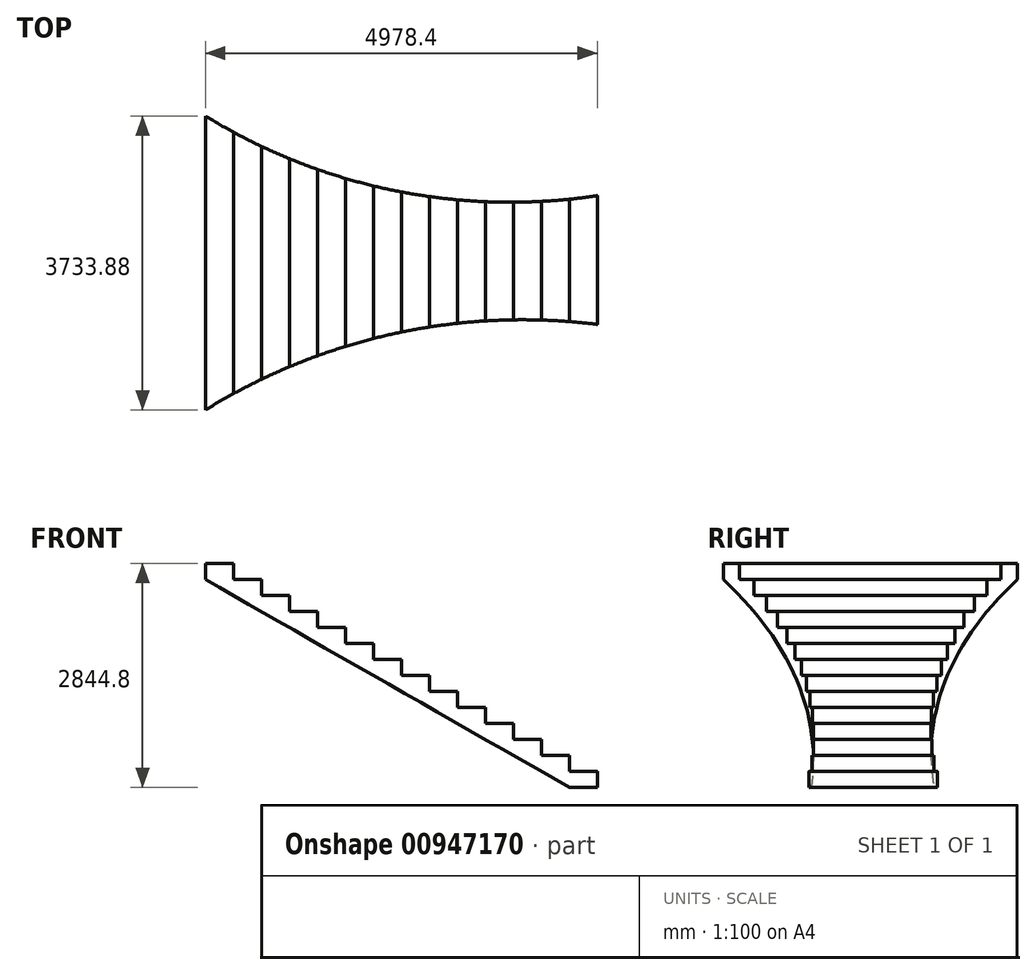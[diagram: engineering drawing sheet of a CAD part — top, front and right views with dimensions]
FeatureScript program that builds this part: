
annotation { "Feature Type Name" : "Feature", "Feature Type Description" : "" }
export const myFeature = defineFeature(function(context is Context, id is Id, definition is map)
    precondition{}
    {
        {
            var Q0;
            Q0=qCreatedBy(makeId("Front.planeOp"),FACE);
            var sketch = newSketch(context, id + "F0", { "sketchPlane" : qUnion([Q0])});
            skLineSegment(sketch, "E0", {"start": v(0, 0) * mm, "end": v(0, 203.2) * mm});
            skLineSegment(sketch, "E1", {"start": v(0, 203.2) * mm, "end": v(-355.6, 203.2) * mm});
            skLineSegment(sketch, "E2", {"start": v(-355.6, 203.2) * mm, "end": v(-355.6, 406.4) * mm});
            skLineSegment(sketch, "E3", {"start": v(-355.6, 406.4) * mm, "end": v(-711.2, 406.4) * mm});
            skLineSegment(sketch, "E4", {"start": v(-711.2, 406.4) * mm, "end": v(-711.2, 609.6) * mm});
            skLineSegment(sketch, "E5", {"start": v(-711.2, 609.6) * mm, "end": v(-1066.8, 609.6) * mm});
            skLineSegment(sketch, "E6", {"start": v(-1066.8, 609.6) * mm, "end": v(-1066.8, 812.8) * mm});
            skLineSegment(sketch, "E7", {"start": v(-1066.8, 812.8) * mm, "end": v(-1422.4, 812.8) * mm});
            skLineSegment(sketch, "E8", {"start": v(-1422.4, 812.8) * mm, "end": v(-1422.4, 1016) * mm});
            skLineSegment(sketch, "E9", {"start": v(-1422.4, 1016) * mm, "end": v(-1778, 1016) * mm});
            skLineSegment(sketch, "E10", {"start": v(-1778, 1016) * mm, "end": v(-1778, 1219.2) * mm});
            skLineSegment(sketch, "E11", {"start": v(-1778, 1219.2) * mm, "end": v(-2133.6, 1219.2) * mm});
            skLineSegment(sketch, "E12", {"start": v(-2133.6, 1219.2) * mm, "end": v(-2133.6, 1422.4) * mm});
            skLineSegment(sketch, "E13", {"start": v(-2133.6, 1422.4) * mm, "end": v(-2489.2, 1422.4) * mm});
            skLineSegment(sketch, "E14", {"start": v(-2489.2, 1422.4) * mm, "end": v(-2489.2, 1625.6) * mm});
            skLineSegment(sketch, "E15", {"start": v(-2489.2, 1625.6) * mm, "end": v(-2844.8, 1625.6) * mm});
            skLineSegment(sketch, "E16", {"start": v(-2844.8, 1625.6) * mm, "end": v(-2844.8, 1828.8) * mm});
            skLineSegment(sketch, "E17", {"start": v(-2844.8, 1828.8) * mm, "end": v(-3200.4, 1828.8) * mm});
            skLineSegment(sketch, "E18", {"start": v(-3200.4, 1828.8) * mm, "end": v(-3200.4, 2032) * mm});
            skLineSegment(sketch, "E19", {"start": v(-3200.4, 2032) * mm, "end": v(-3556, 2032) * mm});
            skLineSegment(sketch, "E20", {"start": v(-3556, 2032) * mm, "end": v(-3556, 2235.2) * mm});
            skLineSegment(sketch, "E21", {"start": v(-3556, 2235.2) * mm, "end": v(-3911.6, 2235.2) * mm});
            skLineSegment(sketch, "E22", {"start": v(-3911.6, 2235.2) * mm, "end": v(-3911.6, 2438.4) * mm});
            skLineSegment(sketch, "E23", {"start": v(-3911.6, 2438.4) * mm, "end": v(-4267.2, 2438.4) * mm});
            skLineSegment(sketch, "E24", {"start": v(-4267.2, 2438.4) * mm, "end": v(-4267.2, 2641.6) * mm});
            skLineSegment(sketch, "E25", {"start": v(-4267.2, 2641.6) * mm, "end": v(-4622.8, 2641.6) * mm});
            skLineSegment(sketch, "E26", {"start": v(-4622.8, 2641.6) * mm, "end": v(-4622.8, 2844.8) * mm});
            skLineSegment(sketch, "E27", {"start": v(-4622.8, 2844.8) * mm, "end": v(-4978.4, 2844.8) * mm});
            skLineSegment(sketch, "E28", {"start": v(0, 0) * mm, "end": v(-355.6, 0) * mm});
            skLineSegment(sketch, "E29", {"start": v(-4978.4, 2844.8) * mm, "end": v(-4978.4, 2641.6) * mm});
            skLineSegment(sketch, "E30", {"start": v(-4978.4, 2641.6) * mm, "end": v(-355.6, 0) * mm});
            skSolve(sketch);
        }
        {
            var Q0;
            Q0 = qSketchRegion(id + "F0", true);
            extrude(context, id + "F1", {"entities" : qUnion([Q0]), "depth" : 3810 * mm, "offsetDistance" : 25.4 * mm});
        }
        {
            var Q0;
            Q0=makeQuery(id+"F1.opExtrude","SWEPT_EDGE",EDGE,{"disambiguationData":[OSD([sQuery(id+"F0.wireOp",EDGE,"E0"),sQuery(id+"F0.wireOp",EDGE,"E1")])]});
            fillet(context, id + "F2", {"entities" : qUnion([Q0]), "radius" : 5.08 * mm, "tangentPropagation" : true, "allowEdgeOverflow" : false});
        }
        {
            var Q0;
            Q0=qCreatedBy(makeId("Top.planeOp"),FACE);
            var sketch = newSketch(context, id + "F3", { "sketchPlane" : qUnion([Q0])});
            skArc(sketch, "E31", {"start": v(0, -2709.93) * mm, "mid": v(-2640.74, -2840.43) * mm, "end": v(-5079.75, -3861.09) * mm});
            skArc(sketch, "E32", {"start": v(-5079.75, 0) * mm, "mid": v(-2637.24, -997.57) * mm, "end": v(0, -1074.7) * mm});
            skLineSegment(sketch, "E33.bottom", {"start": v(-5079.75, -3861.09) * mm, "end": v(0, -3861.09) * mm});
            skLineSegment(sketch, "E33.top", {"start": v(-5079.75, 100.94) * mm, "end": v(0, 100.94) * mm});
            skLineSegment(sketch, "E33.left", {"start": v(-5079.75, -3861.09) * mm, "end": v(-5079.75, 100.94) * mm});
            skLineSegment(sketch, "E33.right", {"start": v(0, -3861.09) * mm, "end": v(0, 100.94) * mm});
            skSolve(sketch);
        }
        {
            var Q0;
            {var subQ0=sQuery(id+"F3.wireOp",EDGE,"E31");Q0=makeQuery(id+"F3.imprint","IMPRINT",FACE,{"disambiguationData":[TD([[makeQuery(id+"F3.imprint","IMPRINT",EDGE,{"derivedFrom":subQ0}),1.0]])]});}
            var Q1;
            {var subQ0=sQuery(id+"F3.wireOp",EDGE,"E32");Q1=makeQuery(id+"F3.imprint","IMPRINT",FACE,{"disambiguationData":[TD([[makeQuery(id+"F3.imprint","IMPRINT",EDGE,{"derivedFrom":subQ0}),1.0]])]});}
            extrude(context, id + "F4", {"entities" : qUnion([Q0, Q1]), "operationType" : NewBodyOperationType.REMOVE, "depth" : 3683 * mm, "offsetDistance" : 25.4 * mm});
        }
    });
